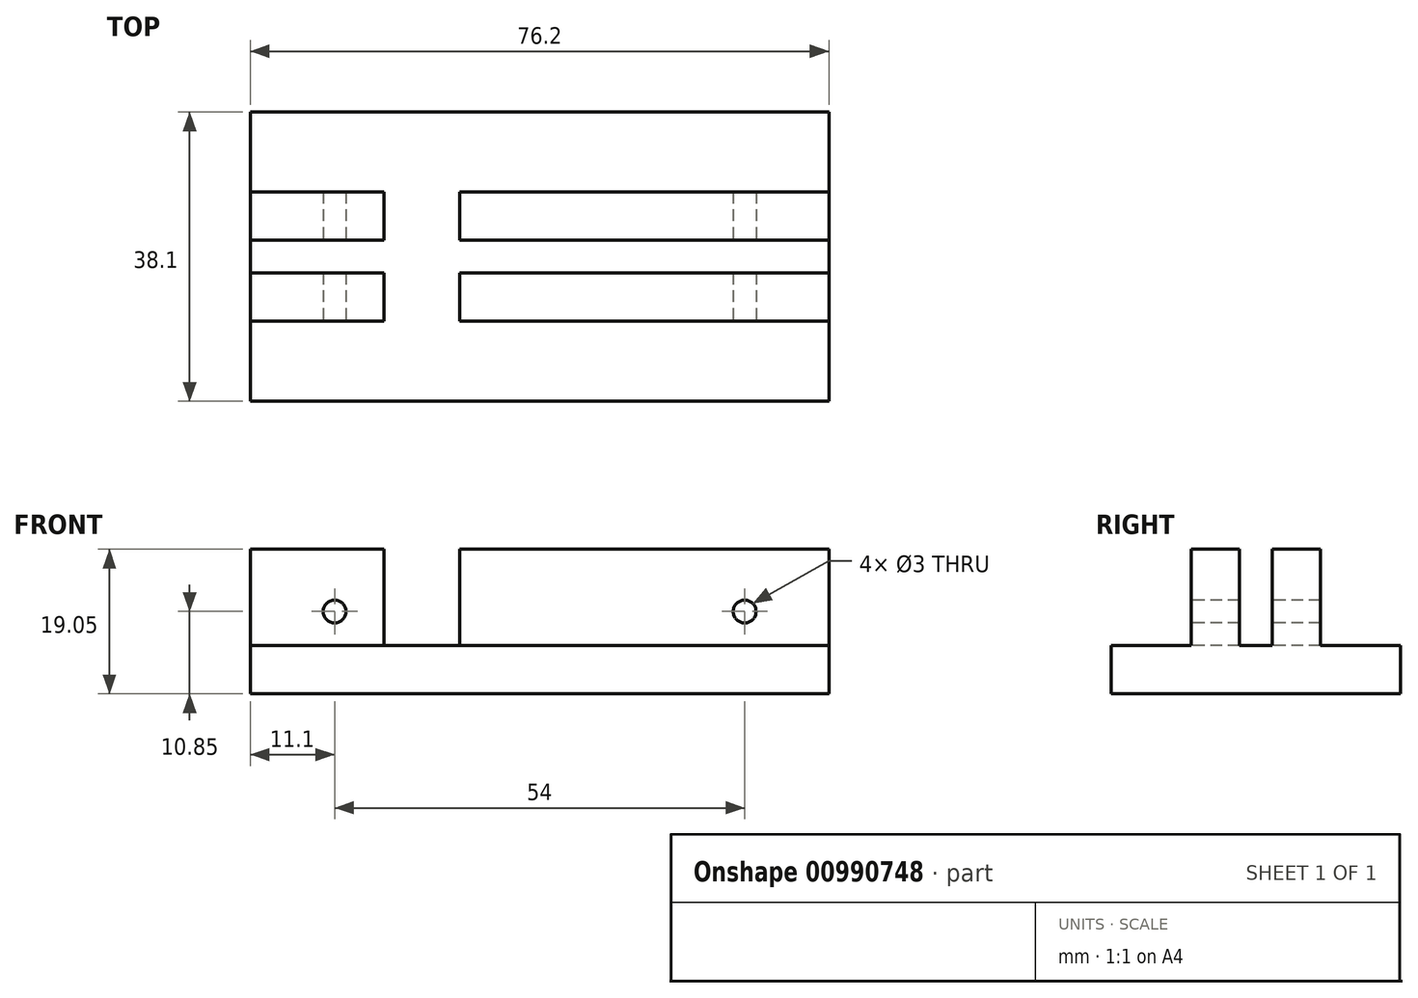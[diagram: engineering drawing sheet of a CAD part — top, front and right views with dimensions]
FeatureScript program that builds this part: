
annotation { "Feature Type Name" : "Feature", "Feature Type Description" : "" }
export const myFeature = defineFeature(function(context is Context, id is Id, definition is map)
    precondition{}
    {
        {
            var Q0;
            Q0=qCreatedBy(makeId("Top.planeOp"),FACE);
            var sketch = newSketch(context, id + "F0", { "sketchPlane" : qUnion([Q0])});
            skLineSegment(sketch, "E0.bottom", {"start": v(-38.1, 19.05) * mm, "end": v(38.1, 19.05) * mm});
            skLineSegment(sketch, "E0.top", {"start": v(-38.1, -19.05) * mm, "end": v(38.1, -19.05) * mm});
            skLineSegment(sketch, "E0.left", {"start": v(-38.1, 19.05) * mm, "end": v(-38.1, -19.05) * mm});
            skLineSegment(sketch, "E0.right", {"start": v(38.1, 19.05) * mm, "end": v(38.1, -19.05) * mm});
            skPoint(sketch, "E1", {"position": v(0, 19.05) * mm});
            skPoint(sketch, "E2", {"position": v(-38.1, 0) * mm});
            skSolve(sketch);
        }
        {
            var Q0;
            Q0=makeQuery(id+"F0.imprint","IMPRINT",FACE,{"disambiguationData":[TD([[makeQuery(id+"F0.imprint","IMPRINT",EDGE,{"derivedFrom":sQuery(id+"F0.wireOp",EDGE,"E0.bottom")}),-1.0]])]});
            extrude(context, id + "F1", {"entities" : qUnion([Q0]), "depth" : 6.35 * mm, "offsetDistance" : 25.4 * mm});
        }
        {
            var Q0;
            Q0=makeQuery(id+"F1.opExtrude","SWEPT_FACE",FACE,{"disambiguationData":[OSD([sQuery(id+"F0.wireOp",EDGE,"E0.right")])]});
            var sketch = newSketch(context, id + "F2", { "sketchPlane" : qUnion([Q0])});
            skLineSegment(sketch, "E3.bottom", {"start": v(-2.16, 0) * mm, "end": v(-8.5, 0) * mm});
            skLineSegment(sketch, "E3.top", {"start": v(-2.16, 19.05) * mm, "end": v(-8.5, 19.05) * mm});
            skLineSegment(sketch, "E3.left", {"start": v(-2.16, 0) * mm, "end": v(-2.16, 19.05) * mm});
            skLineSegment(sketch, "E3.right", {"start": v(-8.5, 0) * mm, "end": v(-8.5, 19.05) * mm});
            skLineSegment(sketch, "E4.MirrorCS", {"start": v(8.5, 0) * mm, "end": v(8.5, 19.05) * mm});
            skLineSegment(sketch, "E5.MirrorCS", {"start": v(2.16, 0) * mm, "end": v(2.16, 19.05) * mm});
            skLineSegment(sketch, "E6.MirrorCS", {"start": v(2.16, 0) * mm, "end": v(8.5, 0) * mm});
            skLineSegment(sketch, "E7.MirrorCS", {"start": v(2.16, 19.05) * mm, "end": v(8.5, 19.05) * mm});
            skSolve(sketch);
        }
        {
            var Q0;
            Q0 = qSketchRegion(id + "F2", true);
            var Q1;
            Q1=makeQuery(id+"F1.opExtrude","SWEPT_FACE",FACE,{"disambiguationData":[OSD([sQuery(id+"F0.wireOp",EDGE,"E0.left")])]});
            extrude(context, id + "F3", {"entities" : qUnion([Q0]), "operationType" : NewBodyOperationType.ADD, "endBound" : BoundingType.UP_TO_SURFACE, "oppositeDirection" : true, "depth" : 25.4 * mm, "endBoundEntityFace" : qUnion([Q1]), "offsetDistance" : 25.4 * mm});
        }
        {
            var Q0;
            Q0=makeQuery(id+"F3.opExtrude","SWEPT_FACE",FACE,{"disambiguationData":[OSD([sQuery(id+"F2.wireOp",EDGE,"E3.right")])]});
            var sketch = newSketch(context, id + "F4", { "sketchPlane" : qUnion([Q0])});
            skLineSegment(sketch, "E8", {"start": v(-27, 10.85) * mm, "end": v(27, 10.85) * mm, "construction": true});
            skPoint(sketch, "E9", {"position": v(0, 10.85) * mm});
            skCircle(sketch, "E10", {"center": v(-27, 10.85) * mm, "radius": 1.5 * mm});
            skCircle(sketch, "E11.MirrorC", {"center": v(27, 10.85) * mm, "radius": 1.5 * mm});
            skLineSegment(sketch, "E12.bottom", {"start": v(-20.5, 6.35) * mm, "end": v(-10.5, 6.35) * mm});
            skLineSegment(sketch, "E12.top", {"start": v(-20.5, 19.05) * mm, "end": v(-10.5, 19.05) * mm});
            skLineSegment(sketch, "E12.left", {"start": v(-20.5, 6.35) * mm, "end": v(-20.5, 19.05) * mm});
            skLineSegment(sketch, "E12.right", {"start": v(-10.5, 6.35) * mm, "end": v(-10.5, 19.05) * mm});
            skSolve(sketch);
        }
        {
            var Q0;
            Q0 = qSketchRegion(id + "F4", true);
            var Q1;
            Q1=makeQuery(id+"F3.opExtrude","SWEPT_FACE",FACE,{"disambiguationData":[OSD([sQuery(id+"F2.wireOp",EDGE,"E4.MirrorCS")])]});
            extrude(context, id + "F5", {"entities" : qUnion([Q0]), "operationType" : NewBodyOperationType.REMOVE, "endBound" : BoundingType.UP_TO_SURFACE, "oppositeDirection" : true, "depth" : 25.4 * mm, "endBoundEntityFace" : qUnion([Q1]), "offsetDistance" : 25.4 * mm});
        }
    });
